# Revit family: ESPO4160
name_source: partatom
category: Allgemeines Modell
units: mm (PartAtom-declared; Revit-internal decimal feet)

## family parameters
Arbeitsebenenbasiert = Nein
Beim Laden mit Abzugskörper schneiden = Nein
Bemaßung runder Anschluss = Durchmesser verwenden
Beschriftungsausrichtung beibehalten = Nein
Gemeinsam genutzt = Nein
Immer vertikal = Ja
Kann Basisbauteil für Bewehrung sein = Nein
Raumberechnungspunkt = Nein
Teiletyp = Normal

## types (1)
- ESPO4160
    Autor = BW
    Bauteilnummer = ESPO
    DocNumber = ESPO%F
    Erstellungsdatum = 29.06.2021
    Folder = ARTIKEL\G5_Bauakustik\G5A_Trittschalldämmung\Egcopal SP\Egcopal SP\
    Genehmigungsdatum Konstr. = 26.07.2021
    Gewicht = 4.468
    Kennung = Artikel
    Konstrukteur = BW
    Konstruktionsstatus = 1
    Revisionsnummer = B
    Status = Freigegeben
    VDS_Category = 3D-Konstruktion Baugruppe
    Vorgabe-Ansicht = 0 mm  [stored 0 ft]

note: [stored X ft] marks values corroborated as IEEE doubles in the binary element streams (Revit-internal decimal feet)
